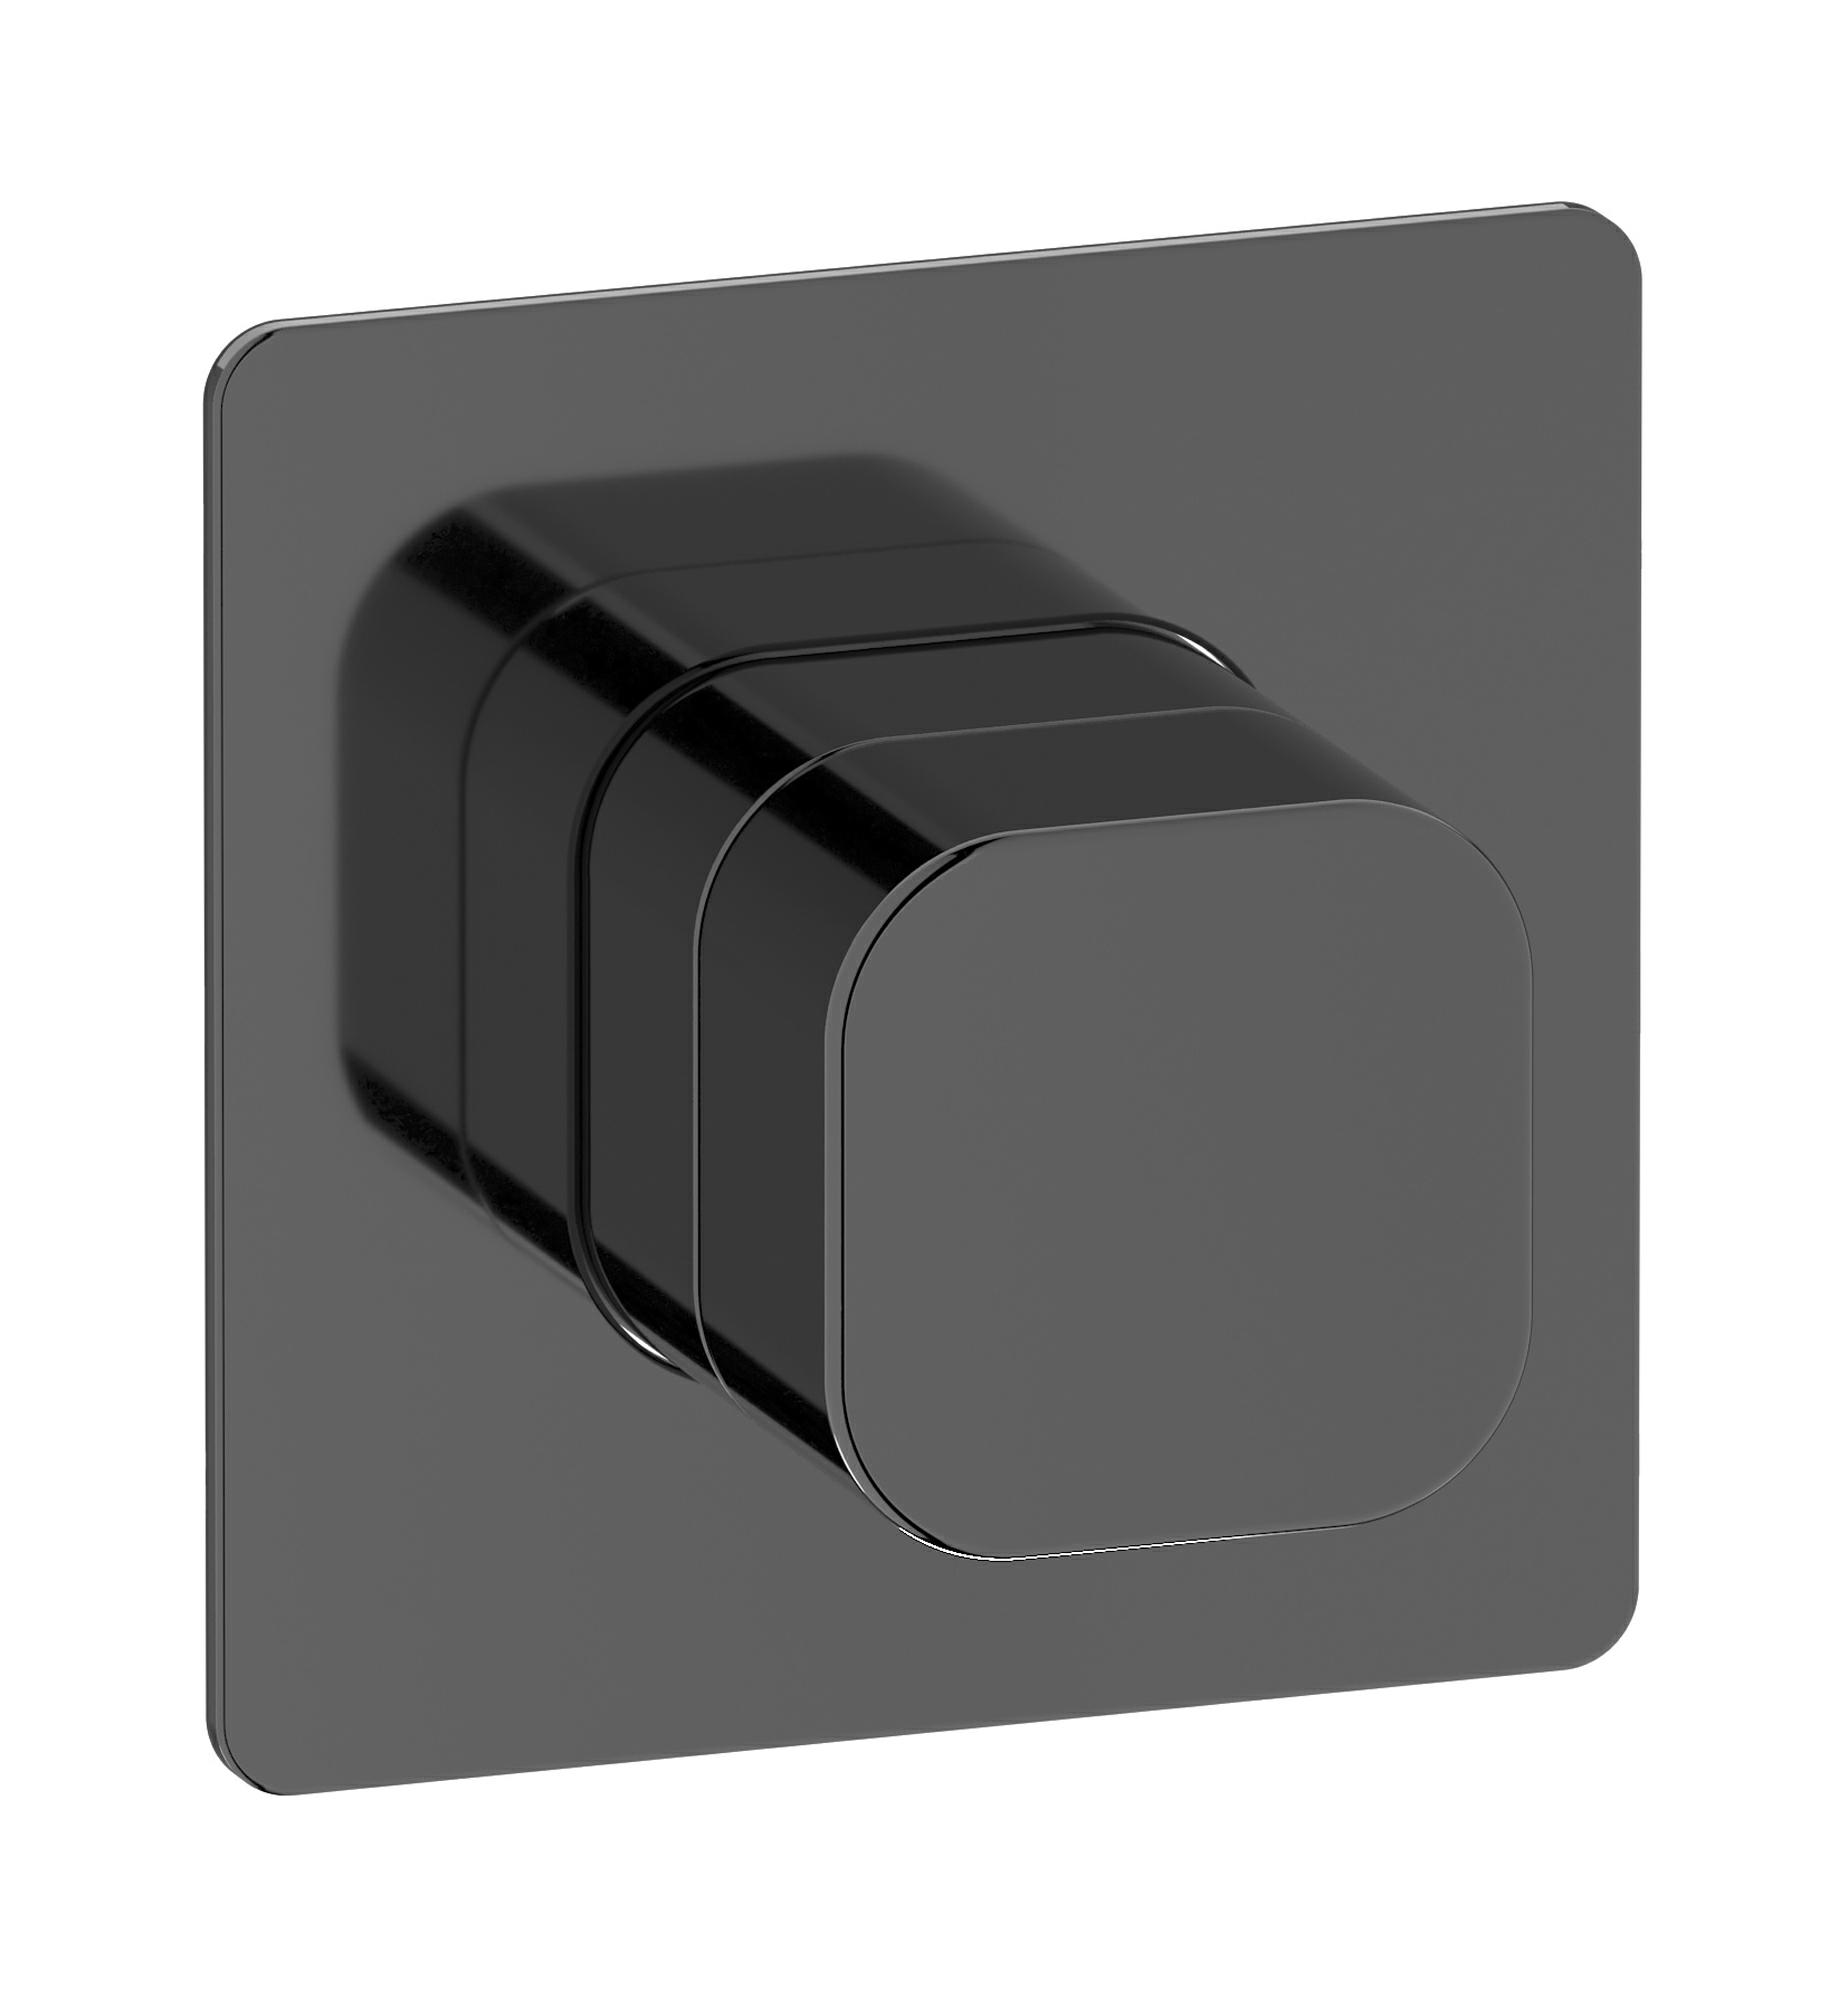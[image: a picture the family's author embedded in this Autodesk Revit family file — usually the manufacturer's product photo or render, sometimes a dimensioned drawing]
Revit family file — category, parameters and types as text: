
# Revit family: EO300_1
name_source: partatom
category: Apparecchi idraulici
units: mm (PartAtom-declared; Revit-internal decimal feet)

## family parameters
Basato su piano di lavoro = No
Condiviso = No
Mantieni orientamento annotazione = No
Numero OmniClass = 23.45.55.17
Punto di calcolo locali = No
Quota connettore circolare = Usa diametro
Sempre verticale = Sì
Taglio con vuoti quando caricato = No
Tipo di parte = Normale
Titolo OmniClass = Mixing Faucets

## types (12) — shared parameters
Cold water inlet = -10 mm  [stored -0.0328084 ft]
Commenti sul tipo = Shower mixer
Connessione CW = No
Connessione HW = No
Connessione di scarico = No
Connessione di ventilazione = No
Descrizione = One way shower mixer
Hot water inlet = 10 mm  [stored 0.0328084 ft]
Produttore = IB Rubinetterie S.p.A.
URL = https://www.weareib.it
zero-valued in all types: Prospetto di default

## per-type parameters (varying)
| type | Finishes surface | Immagine tipo | Modello |
| Chrome | IB_Chrome | EO300CC_1.jpg | EO300CC_1 |
| Brushed nickel | IB_Brushed nickel | EO300SS_1.jpg | EO300SS_1 |
| Natural brass | IB_Brass | EO300ON_1.jpg | EO300ON_1 |
| Matt black | IB_matt black | EO300NP_1.jpg | EO300NP_1 |
| Black chrome | IB_Black chrome | EO300CF_1.jpg | EO300CF_1 |
| Brushed black chrome | IB_Brushed black chrome | EO300CS_1.jpg | EO300CS_1 |
| Pale gold | IB_Pale gold | EO300II_1.jpg | EO300II_1 |
| Brushed pale gold | IB_brushed pale gold | EO300IS_1.jpg | EO300IS_1 |
| Rose gold | IB_Rose gold | EO300RS_1.jpg | EO300RS_1 |
| Brushed rose gold | IB_Brushed rose gold | EO300SR_1.jpg | EO300SR_1 |
| Gold | IB_gold | EO300OO_1.jpg | EO300OO_1 |
| Brushed gold | IB_brushed gold | EO300OS_1.jpg | EO300OS_1 |

note: [stored X ft] marks values corroborated as IEEE doubles in the binary element streams (Revit-internal decimal feet)
